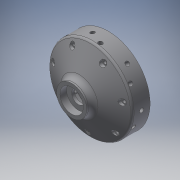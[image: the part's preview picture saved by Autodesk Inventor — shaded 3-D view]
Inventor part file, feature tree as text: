
AUTODESK INVENTOR PART (.ipt)
format: ipt  version: 2018 (Build 220112000, 112)  size: 404,992 bytes
history: native  units: mm
features: sketch x5, revolve x2, extrude x2, hole x1, other x1, pattern_circular x1, projected_geometry x1
ambient origin geometry x8: Origin, YZ Plane, XZ Plane, XY Plane, X Axis, Y Axis, Z Axis, Center Point
bodies: Solid1 (feature_tree)
feature tree (13):
  revolve  "Revolution1"  [1 undecoded]
  extrude  "Extrusion1"  Depth=6.0mm
  hole  "Hole1"  [1 undecoded]
  revolve  "Revolution2"  [1 undecoded]
  extrude  "Extrusion2"  Depth=10.0mm
  other  "Work Axis1"
  pattern_circular  "Circular Pattern1"  [2 undecoded]
  sketch  "Sketch1"  dims[d0=50.0mm d1=45.0mm]
  sketch  "Sketch2"  dims[d2=40.5mm d3=6.0mm]
  sketch  "Sketch3"  dims[d4=32.5mm d5=44.0mm]
  sketch  "Sketch4"  dims[d6=3.5mm d7=18.0mm]
  sketch  "Sketch5"  dims[d8=14.0mm d9=4.63734mm d10=8.0mm d11=3.5mm d12=8.0mm d13=3.0mm d14=90.0deg d15=5.0mm d16=7.0mm d17=9.0mm d18=10.0mm d19=16.5mm d20=59.5mm d21=0.0mm d23=4.0mm d24=6.0mm d25=4.0mm d26=2.0mm d27=90.0deg d28=24.5mm d29=0.0mm d30=3.5mm d32=5.0mm d33=90.0deg d34=70.0mm d35=360.0deg d37=21.0mm d38=42.5mm d39=5.0mm d40=10.0mm d41=0.0mm d42=22.5mm]
  projected_geometry  "Projected Loop1"
note: 5 required parameter values undecoded (feature->parameter linkage not recoverable at this tier; creation-order binding heuristic only, values carry confidence <= 0.55)